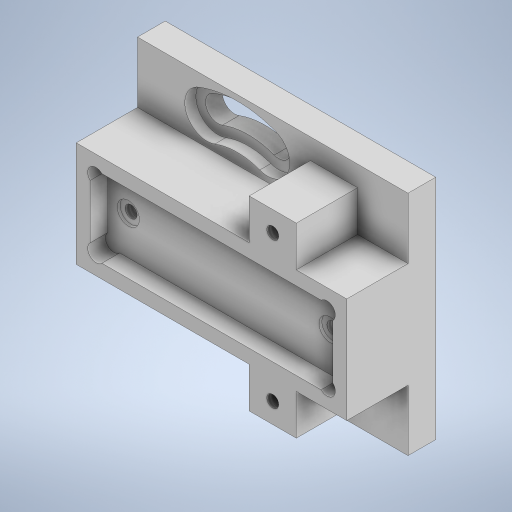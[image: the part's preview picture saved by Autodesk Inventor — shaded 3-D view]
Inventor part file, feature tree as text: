
AUTODESK INVENTOR PART (.ipt)
format: ipt  version: 2024.2 (Build 282272000, 272)  size: 517,632 bytes
history: native  units: in
note: dims shown in document units (in); Inventor stores cm internally (conversion verified against a paired STEP export)
features: extrude x11, hole x7, sketch x7, chamfer x1
ambient origin geometry x8: Origin, YZ Plane, XZ Plane, XY Plane, X Axis, Y Axis, Z Axis, Center Point
bodies: Solid1 (feature_tree)
feature tree (26):
  extrude  "Extrusion1"  TaperAngle=0.0deg  [1 undecoded]
  hole  "Hole1"  [1 undecoded]
  hole  "Hole2"  [1 undecoded]
  hole  "Hole3"  [1 undecoded]
  extrude  "Extrusion2"  Depth=0.0394in
  extrude  "Extrusion3"  TaperAngle=0.0deg  [1 undecoded]
  hole  "Hole5"  [1 undecoded]
  hole  "Hole6"  [1 undecoded]
  extrude  "Extrusion4"  Depth=0.0413in
  extrude  "Extrusion6"  Depth=0.0827in TaperAngle=0.0deg
  chamfer  "Chamfer5"  Distance=1.9213in
  sketch  "Sketch12"  dims[d2=0.5059in d3=0.0in]
  extrude  "Extrusion12"  Depth=1.6142in
  extrude  "Extrusion13"  Depth=0.1969in TaperAngle=0.0deg
  hole  "Hole7"  [1 undecoded]
  sketch  "Sketch15"  dims[d12=0.0in d13=1.4331in]
  sketch  "Sketch17"  dims[d14=0.7165in]
  extrude  "Extrusion14"  TaperAngle=0.0deg  [1 undecoded]
  extrude  "Extrusion15"  TaperAngle=0.0deg  [1 undecoded]
  extrude  "Extrusion16"  TaperAngle=0.0deg  [1 undecoded]
  extrude  "Extrusion17"  Depth=0.0197in
  hole  "Hole8"  [1 undecoded]
  sketch  "Sketch14"  dims[d4=0.0849in d5=0.224in d6=0.1575in d7=0.0787in d8=90.0deg d9=0.3492in d10=0.0in d11=0.0in]
  sketch  "Sketch19"  dims[d15=0.1772in d16=0.224in d17=0.315in d18=0.3445in d19=0.5635in d20=0.3492in d21=0.0in d22=0.0in]
  sketch  "Sketch20"  dims[d23=0.0in d24=0.0394in]
  sketch  "Sketch21"  dims[d25=0.0in d26=0.0in d27=0.3937in d28=0.1969in d29=0.0413in d30=0.0827in d31=0.224in d32=0.315in d33=0.1654in d34=0.5635in d35=0.0827in d36=0.0in d37=0.0827in d38=0.0in d39=1.9213in d40=1.6142in d41=0.1969in d42=0.0in d54=0.0in d55=0.0in d56=0.0in d57=0.0in d58=0.1575in d59=0.224in d60=0.315in d61=0.0787in d62=0.5635in d63=0.0197in d64=0.0in d77=0.0394in d78=0.0413in d79=0.3937in d80=0.0in d81=0.0in d82=0.1969in d83=0.0827in d84=0.224in d85=0.315in d86=0.0787in d87=0.5635in d88=0.0827in d89=0.0in d90=0.0827in d91=0.0in d97=1.9213in d98=0.748in d99=1.7244in d100=0.5512in d101=0.126in d102=0.0in d103=0.0394in d104=0.0787in d105=45.0deg d106=0.1181in d107=45.0deg d108=45.0deg d109=45.0deg d110=0.1181in d111=0.1181in d112=0.1181in d118=0.315in d122=0.1772in d129=0.0in d130=0.0in d131=0.0787in d132=0.0in d133=0.0827in d134=0.2362in d135=0.1575in d136=0.0787in d137=90.0deg d138=0.0827in d139=0.0in d140=1.5354in d141=0.9055in d142=1.3976in d143=1.0433in d147=0.315in d148=0.1772in d149=0.1772in d150=0.315in d151=0.0in d152=0.0in d153=0.0787in d154=0.0in d155=0.3583in d156=0.3346in d157=0.2874in d158=0.435in d159=0.0in d160=0.3583in d161=0.3346in d162=0.2874in d163=0.435in d164=0.0in d165=0.1437in d166=0.0849in d167=0.224in d168=0.1575in d169=0.0787in d170=90.0deg d171=0.3492in d172=0.0in d127=0.0197in d128=0.0344in]
note: 12 required parameter values undecoded (feature->parameter linkage not recoverable at this tier; creation-order binding heuristic only, values carry confidence <= 0.55)
